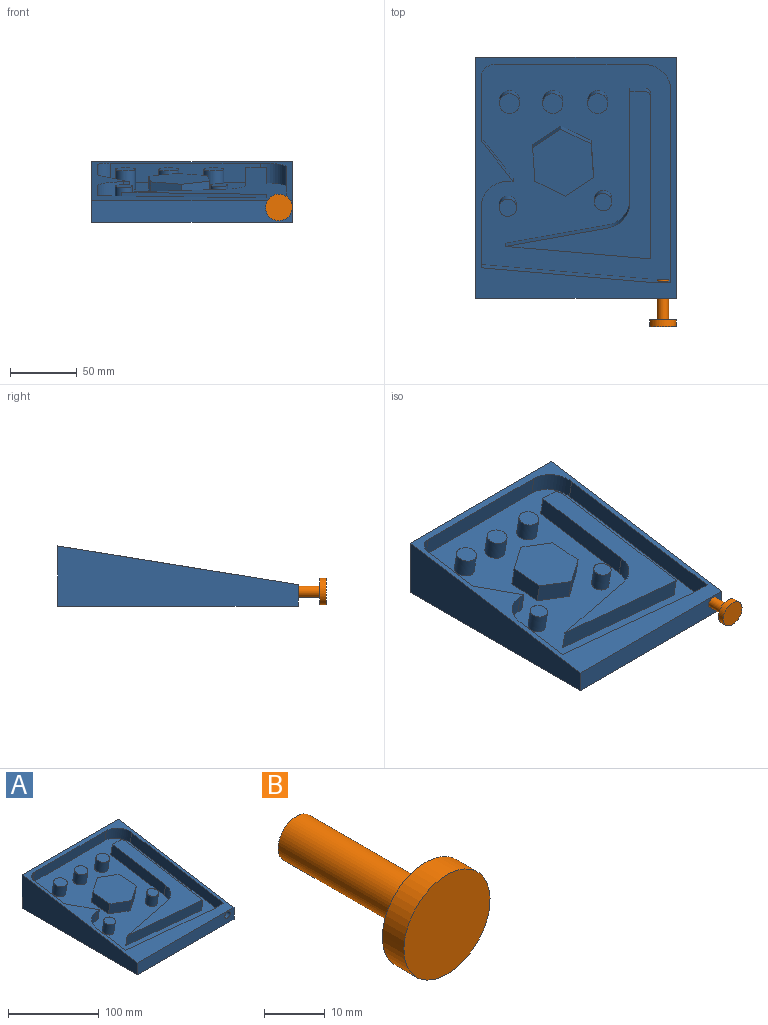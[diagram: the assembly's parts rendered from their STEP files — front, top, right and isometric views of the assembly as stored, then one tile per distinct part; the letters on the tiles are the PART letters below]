
ASSEMBLY  parts=2 mates=1
PART A: 44 faces, bbox 150.3x180.3x45.3 mm
  f0: plane 162.9x142mm, normal (0,-0.16,0.99), area 16513.3mm2, adj f1,f2,f3,f10,f11,f12,f13,f14
  f1: plane 47.31x22.05mm, normal (1,0,0), area 682.6mm2, adj f0,f6,f22,f37
  f2: plane 15.29x15.1mm, normal (0,0.99,0.16), area 167.5mm2, adj f0,f3,f6,f22,f43
  f3: plane 145.54x37.87mm, normal (-1,0,0), area 2175mm2, adj f0,f2,f6,f21
  f4: plane 180x150mm, normal (0,0,-1), area 27000mm2, adj f5,f7,f8,f9
  f5: plane 150x45mm, normal (0,1,0), area 6750mm2, adj f4,f6,f8,f9
  f6: plane 180x150mm, normal (0,-0.16,0.99), area 5181.5mm2, adj f1,f2,f3,f5,f7,f8,f9,f10
  f7: plane 150x16mm, normal (0,-1,0), area 2343.3mm2, adj f4,f6,f8,f9,f43
  f8: plane 180x45mm, normal (1,0,0), area 5490mm2, adj f4,f5,f6,f7
  f9: plane 180x45mm, normal (-1,0,0), area 5490mm2, adj f4,f5,f6,f7
  f10: cylinder r=10mm len=16.4mm, axis (0,-0.16,0.99), area 235.6mm2, adj f0,f6,f11,f12
  f11: plane 49.44x22.39mm, normal (1,0,0), area 714.9mm2, adj f0,f6,f10,f36
  f12: plane 112x14.81mm, normal (0,-0.99,-0.16), area 1680mm2, adj f0,f6,f10,f21
  f13: plane 108.43x16.31mm, normal (-0.09,-0.98,-0.16), area 1632.7mm2, adj f0,f14,f19,f20
  f14: plane 122.8x34.21mm, normal (1,0,0), area 1829.4mm2, adj f0,f13,f15,f20
  f15: cylinder r=5mm len=15.6mm, axis (0,0.16,-0.99), area 117.8mm2, adj f0,f14,f16,f20
  f16: plane 14.81x10.68mm, normal (0,0.99,0.16), area 160.1mm2, adj f0,f15,f17,f20
  f17: plane 85.31x28.17mm, normal (-1,0,0), area 1259.9mm2, adj f0,f16,f18,f20
  f18: cylinder r=20mm len=21.81mm, axis (0,0.16,-0.99), area 417.4mm2, adj f0,f17,f19,f20
  f19: plane 76.33x17.01mm, normal (-0.18,0.97,0.16), area 1163.7mm2, adj f0,f13,f18,f20
  f20: plane 125.35x108.43mm, normal (0,-0.16,0.99), area 3185.2mm2, adj f13,f14,f15,f16,f17,f18,f19
  f21: cylinder r=20mm len=22.13mm, axis (0,0.16,-0.99), area 471.2mm2, adj f0,f3,f6,f12
  f22: plane 127x16.57mm, normal (0.09,0.98,0.16), area 1912.2mm2, adj f0,f1,f2,f6
  f23: plane 22.78x16.59mm, normal (0.44,0.89,0.14), area 380.6mm2, adj f0,f24,f28,f29
  f24: plane 21.06x17.06mm, normal (-0.56,0.82,0.13), area 380.6mm2, adj f0,f23,f25,f29
  f25: plane 27.38x18.84mm, normal (-1,-0.07,-0.01), area 380.6mm2, adj f0,f24,f26,f29
  f26: plane 22.78x16.59mm, normal (-0.44,-0.89,-0.14), area 380.6mm2, adj f0,f25,f27,f29
  f27: plane 21.06x17.06mm, normal (0.56,-0.82,-0.13), area 380.6mm2, adj f0,f26,f28,f29
  f28: plane 27.38x18.84mm, normal (1,0.07,0.01), area 380.6mm2, adj f0,f23,f27,f29
  f29: plane 49.98x45.57mm, normal (0,-0.16,0.99), area 1672.5mm2, adj f23,f24,f25,f26,f27,f28
  f30: cylinder r=7.5mm len=17.2mm, axis (0,0.16,-0.99), area 706.9mm2, adj f0,f31
  f31: plane 15x14.81mm, normal (0,-0.16,0.99), area 176.7mm2, adj f30
  f32: cylinder r=7.5mm len=17.2mm, axis (0,0.16,-0.99), area 706.9mm2, adj f0,f33
  f33: plane 15x14.81mm, normal (0,-0.16,0.99), area 176.7mm2, adj f32
  f34: cylinder r=7.5mm len=17.2mm, axis (0,0.16,-0.99), area 706.9mm2, adj f0,f35
  f35: plane 15x14.81mm, normal (0,-0.16,0.99), area 176.7mm2, adj f34
  f36: plane 32.78x23.94mm, normal (0.79,0.61,0.1), area 584.9mm2, adj f0,f6,f11,f38
  f37: cylinder r=20mm len=22.13mm, axis (0,0.16,-0.99), area 471.2mm2, adj f0,f1,f6,f38
  f38: plane 14.81x3.94mm, normal (0,-0.99,-0.16), area 59.1mm2, adj f0,f6,f36,f37
  f39: cylinder r=6.5mm len=16.88mm, axis (0,0.16,-0.99), area 612.6mm2, adj f0,f40
  f40: plane 13x12.83mm, normal (0,-0.16,0.99), area 132.7mm2, adj f39
  f41: cylinder r=6.5mm len=16.88mm, axis (0,0.16,-0.99), area 612.6mm2, adj f0,f42
  f42: plane 13x12.83mm, normal (0,-0.16,0.99), area 132.7mm2, adj f41
  f43: cylinder r=4.25mm len=13.6mm, axis (0,-1,0), area 345mm2, adj f2,f7
PART B: 5 faces, bbox 20x35x20 mm
  f0: cylinder r=4.25mm len=30mm, axis (0,1,0), area 801.1mm2, adj f1,f4
  f1: plane 8.5x8.5mm, normal (0,1,0), area 56.7mm2, adj f0
  f2: cylinder r=10mm len=20mm, axis (0,1,0), area 314.2mm2, adj f3,f4
  f3: plane 20x20mm, normal (0,-1,0), area 314.2mm2, adj f2
  f4: plane 20x20mm, normal (0,1,0), area 257.4mm2, adj f0,f2
PLACE A t=(-75,93.32,0)mm
PLACE B t=(-111.53,13.82,36.74)mm
MATE slider B.f0 <-> A.f43  axis (0,1,0) through (-10,13.82,11)mm
